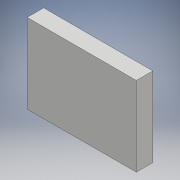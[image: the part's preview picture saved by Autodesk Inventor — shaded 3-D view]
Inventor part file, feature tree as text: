
AUTODESK INVENTOR PART (.ipt)
format: ipt  version: 2018 (Build 220112000, 112)  size: 88,576 bytes
history: native  units: mm
features: sketch x2, extrude x1
ambient origin geometry x8: Origin, YZ Plane, XZ Plane, XY Plane, X Axis, Y Axis, Z Axis, Center Point
bodies: 实体1 (feature_tree)
feature tree (3):
  extrude  "拉伸1"  Depth=33.0mm
  sketch  "草图2"  dims[d2=5.0mm d3=0.0mm]
  sketch  "草图1"  dims[d0=24.0mm d1=33.0mm]
